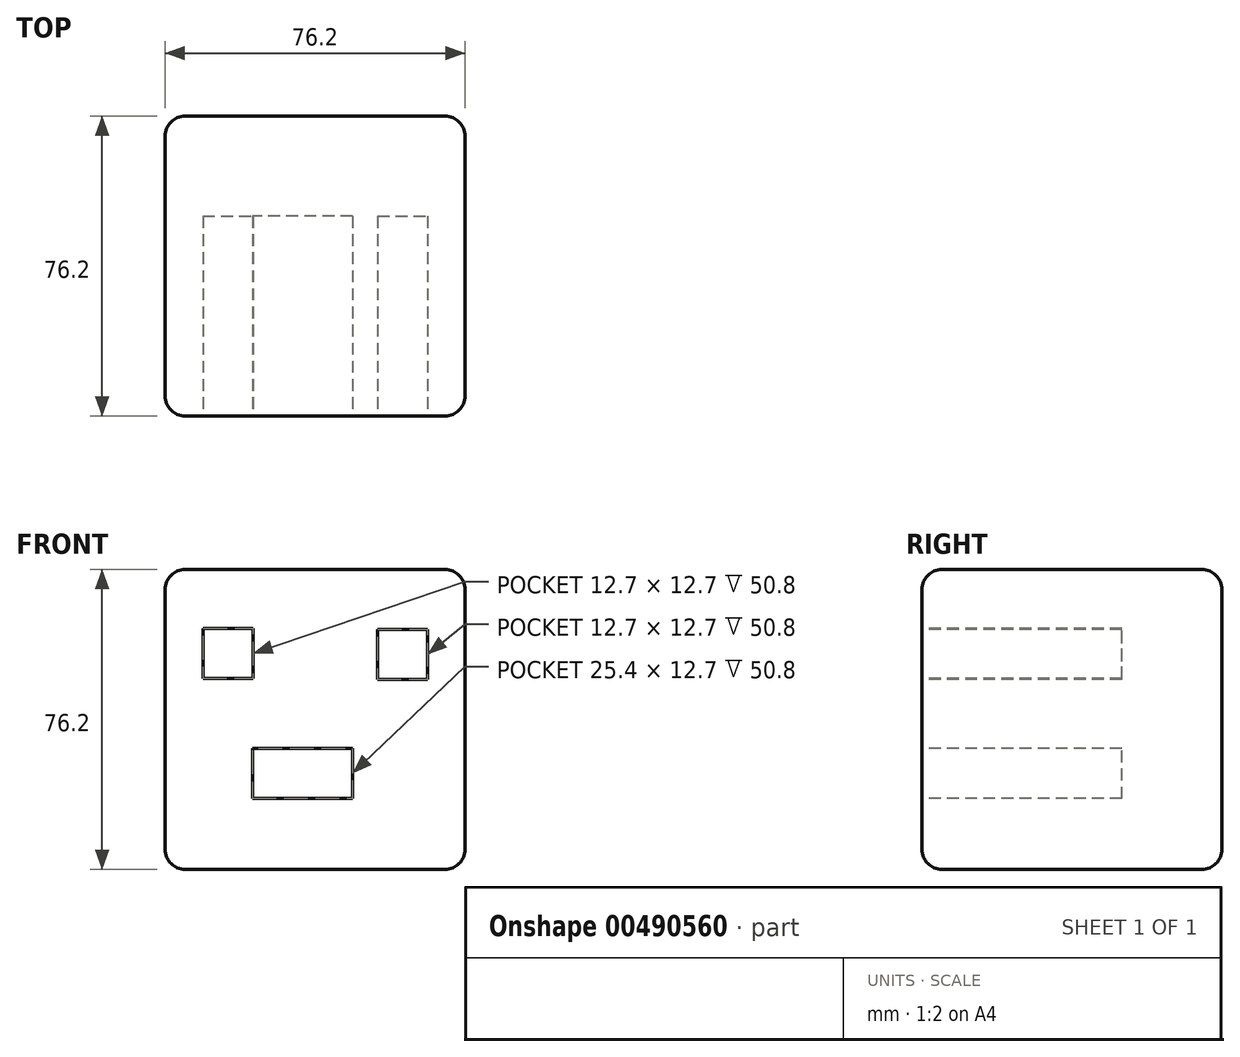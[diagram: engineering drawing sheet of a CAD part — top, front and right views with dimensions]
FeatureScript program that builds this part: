
annotation { "Feature Type Name" : "Feature", "Feature Type Description" : "" }
export const myFeature = defineFeature(function(context is Context, id is Id, definition is map)
    precondition{}
    {
        {
            var Q0;
            Q0=qCreatedBy(makeId("Front.planeOp"),FACE);
            var sketch = newSketch(context, id + "F0", { "sketchPlane" : qUnion([Q0])});
            skLineSegment(sketch, "E0.bottom", {"start": v(0, 0) * mm, "end": v(-76.2, 0) * mm});
            skLineSegment(sketch, "E0.top", {"start": v(0, 76.2) * mm, "end": v(-76.2, 76.2) * mm});
            skLineSegment(sketch, "E0.left", {"start": v(0, 0) * mm, "end": v(0, 76.2) * mm});
            skLineSegment(sketch, "E0.right", {"start": v(-76.2, 0) * mm, "end": v(-76.2, 76.2) * mm});
            skSolve(sketch);
        }
        {
            var Q0;
            Q0 = qSketchRegion(id + "F0", true);
            extrude(context, id + "F1", {"entities" : qUnion([Q0]), "depth" : 76.2 * mm});
        }
        {
            var Q0;
            Q0=makeQuery(id+"F1.opExtrude","CAP_FACE",FACE,{"disambiguationData":[OSD([sQuery(id+"F0.wireOp",EDGE,"E0.bottom"),sQuery(id+"F0.wireOp",EDGE,"E0.top"),sQuery(id+"F0.wireOp",EDGE,"E0.left"),sQuery(id+"F0.wireOp",EDGE,"E0.right")])],"isStart":false});
            var sketch = newSketch(context, id + "F2", { "sketchPlane" : qUnion([Q0])});
            skLineSegment(sketch, "E1.bottom", {"start": v(-66.58, 48.55) * mm, "end": v(-53.88, 48.55) * mm});
            skLineSegment(sketch, "E1.top", {"start": v(-66.58, 61.25) * mm, "end": v(-53.88, 61.25) * mm});
            skLineSegment(sketch, "E1.left", {"start": v(-66.58, 48.55) * mm, "end": v(-66.58, 61.25) * mm});
            skLineSegment(sketch, "E1.right", {"start": v(-53.88, 48.55) * mm, "end": v(-53.88, 61.25) * mm});
            skPoint(sketch, "E1.middle", {"position": v(-60.23, 54.9) * mm});
            skLineSegment(sketch, "E2.bottom", {"start": v(-22.22, 48.23) * mm, "end": v(-9.52, 48.23) * mm});
            skLineSegment(sketch, "E2.top", {"start": v(-22.22, 60.93) * mm, "end": v(-9.52, 60.93) * mm});
            skLineSegment(sketch, "E2.left", {"start": v(-22.22, 48.23) * mm, "end": v(-22.22, 60.93) * mm});
            skLineSegment(sketch, "E2.right", {"start": v(-9.52, 48.23) * mm, "end": v(-9.52, 60.93) * mm});
            skLineSegment(sketch, "E3.bottom", {"start": v(-28.6, 18) * mm, "end": v(-54, 18) * mm});
            skLineSegment(sketch, "E3.top", {"start": v(-28.6, 30.7) * mm, "end": v(-54, 30.7) * mm});
            skLineSegment(sketch, "E3.left", {"start": v(-28.6, 18) * mm, "end": v(-28.6, 30.7) * mm});
            skLineSegment(sketch, "E3.right", {"start": v(-54, 18) * mm, "end": v(-54, 30.7) * mm});
            skSolve(sketch);
        }
        {
            var Q0;
            Q0=makeQuery(id+"F1.opExtrude","CAP_FACE",FACE,{"disambiguationData":[OSD([sQuery(id+"F0.wireOp",EDGE,"E0.bottom"),sQuery(id+"F0.wireOp",EDGE,"E0.top"),sQuery(id+"F0.wireOp",EDGE,"E0.left"),sQuery(id+"F0.wireOp",EDGE,"E0.right")])],"isStart":false});
            var Q1;
            Q1=makeQuery(id+"F1.opExtrude","SWEPT_FACE",FACE,{"disambiguationData":[OSD([sQuery(id+"F0.wireOp",EDGE,"E0.left")])]});
            var Q2;
            Q2=makeQuery(id+"F1.opExtrude","SWEPT_FACE",FACE,{"disambiguationData":[OSD([sQuery(id+"F0.wireOp",EDGE,"E0.right")])]});
            var Q3;
            Q3=makeQuery(id+"F1.opExtrude","CAP_FACE",FACE,{"disambiguationData":[OSD([sQuery(id+"F0.wireOp",EDGE,"E0.bottom"),sQuery(id+"F0.wireOp",EDGE,"E0.top"),sQuery(id+"F0.wireOp",EDGE,"E0.left"),sQuery(id+"F0.wireOp",EDGE,"E0.right")])],"isStart":true});
            fillet(context, id + "F3", {"entities" : qUnion([Q0, Q1, Q2, Q3]), "radius" : 5.08 * mm, "tangentPropagation" : true, "allowEdgeOverflow" : false});
        }
        {
            var Q0;
            Q0 = qSketchRegion(id + "F2", true);
            extrude(context, id + "F4", {"entities" : qUnion([Q0]), "operationType" : NewBodyOperationType.REMOVE, "oppositeDirection" : true, "depth" : 50.8 * mm});
        }
    });
